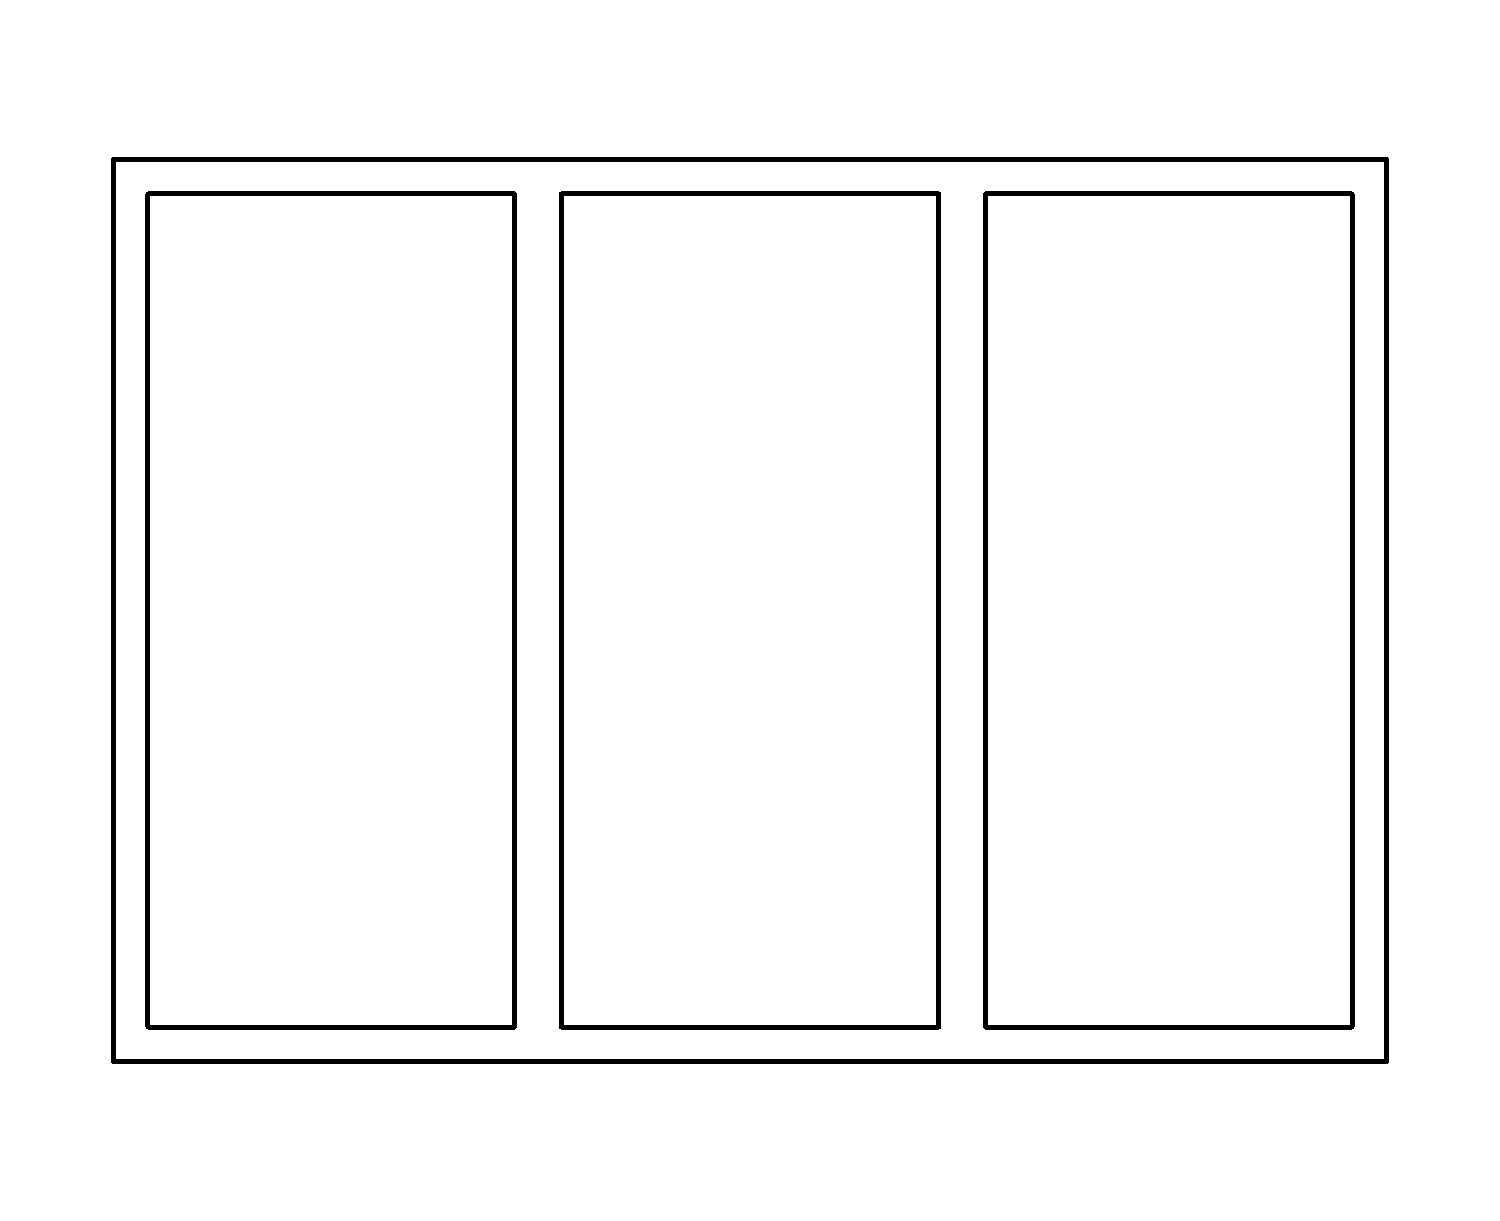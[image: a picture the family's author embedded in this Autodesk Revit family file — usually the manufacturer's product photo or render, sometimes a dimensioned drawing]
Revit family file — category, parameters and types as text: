
# Revit family: окна.rehau_трехпольное
name_source: partatom
category: Окна
revit_build: Autodesk Revit 2017 (Build: 20171027_0315(x64)
units: mm (PartAtom-declared; Revit-internal decimal feet)

## family parameters
Всегда вертикально = Да
Заголовок OmniClass = Windows
Номер OmniClass = 23.30.20.00
Общий = Нет
Основа = Стена
При загрузке вырезать с полостями = Нет
Точка расчета площади = Нет

## types (2) — shared parameters
24_мм = 24мм 1-камерный
32_мм = 32мм 2-камерный
40_мм = 40мм 2-камерный
42_мм = 42мм 2-камерный
50_мм = 50мм 2-камерный
60_blitz_new = 60 BLITZ NEW
60_euro_64 = 60 EURO (коробка 64, импост 78, створка 60)
60_euro_68 = 60 EURO (коробка 68, импост 78, створка 60)
60_euro_76 = 60 EURO (коробка 76, импост 86, створка 74)
70_delight_78 = 70 DELIGHT
70_grazio_55 = 70 GRAZIO (коробка 55)
70_grazio_63 = 70 GRAZIO (коробка 63)
80_intelio_58r = 80 INTELIO (коробка 58, створка R57)
80_intelio_58z = 80 INTELIO (коробка 58, створка Z57)
80_intelio_65r = 80 INTELIO (коробка 65, створка R57)
80_intelio_65z = 80 INTELIO (коробка 65, створка Z57)
ADSK_Обозначение = ГОСТ 30674-99
URL = https://www.rehau.com
sp_energy = Энергосберегающие стекла
sp_gaz = Заполненный газом
sp_standart = Обычный стеклопакет
sp_triplex = Триплекс
Аналитическая конструкция = Окна с одинарным остеклением - для жилых зданий
Высота подоконника по умолчанию = 900 мм
Группа модели = ОП
Длина профилей коробки = 7040 мм
Замыкание стены = По основе
Изготовитель = Rehau
Изображение типоразмера = схема_трехпольное.png
Коэффициент теплопередачи (U) = 5.7361 Вт/(м²·K)
Коэффициент теплопритока от солнечного излучения = 0.86
Материал коробки = <По категории>
Материал отлива = <По категории>
Материал подоконника = <По категории>
Материал стекла = <По категории>
Описание = проем.окно
Примерная высота = 1460 мм
Примерная ширина = 2060 мм
Пропускание видимого света = 0.9
Равные створки = Да
Створка слева = 400 мм
Створка справа = 400 мм
Термостойкость = 0.1743 (м²·K)/Вт
Тип створки центр = створка : глухая
глухая_створка = створка : глухая
обозначение_проема_высота = 243 мм
обозначение_проема_ширина = 343 мм
створка_слева_размер = 687 мм
створка_справа_размер = 687 мм
таблица выбора = каталог профилей Rehau

## per-type parameters (varying)
| type | Тип створки слева | Тип створки справа |
| 2060х1460 (створка и глухое) | створка : левая-откидная | створка : правая-откидная |
| 2060х1460 (глухое) | створка : глухая | створка : глухая |
